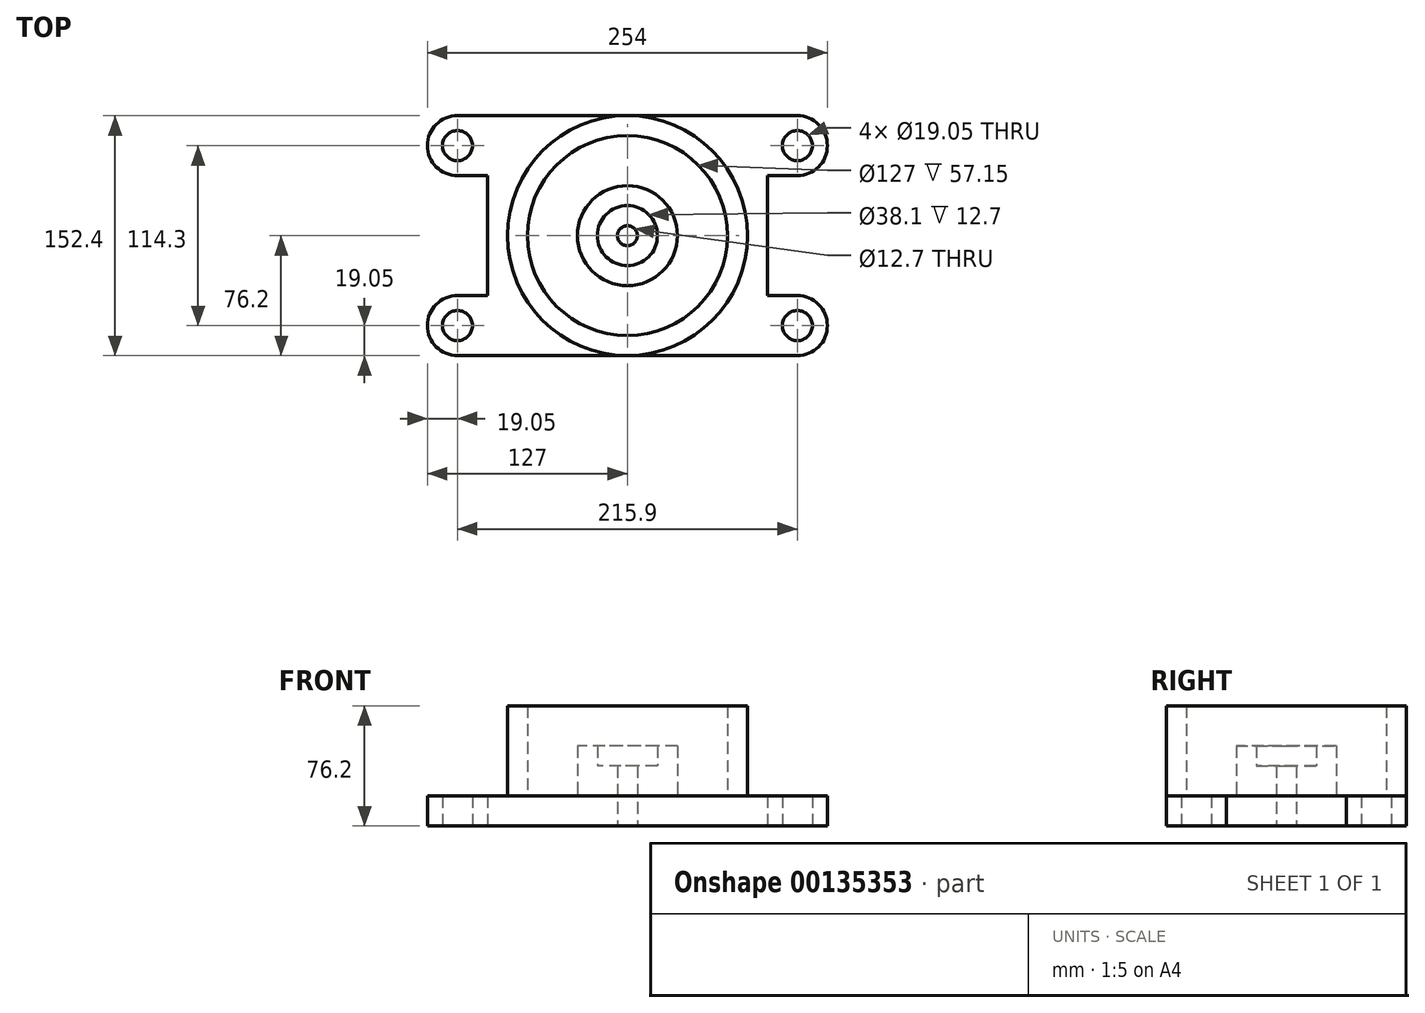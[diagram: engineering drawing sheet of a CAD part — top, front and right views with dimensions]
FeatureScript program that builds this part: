
annotation { "Feature Type Name" : "Feature", "Feature Type Description" : "" }
export const myFeature = defineFeature(function(context is Context, id is Id, definition is map)
    precondition{}
    {
        {
            var Q0;
            Q0=qCreatedBy(makeId("Top.planeOp"),FACE);
            var sketch = newSketch(context, id + "F0", { "sketchPlane" : qUnion([Q0])});
            skCircle(sketch, "E0", {"center": v(0, 0) * mm, "radius": 6.35 * mm});
            skCircle(sketch, "E1", {"center": v(0, 0) * mm, "radius": 19.05 * mm});
            skCircle(sketch, "E2", {"center": v(0, 0) * mm, "radius": 31.75 * mm});
            skCircle(sketch, "E3", {"center": v(0, 0) * mm, "radius": 63.5 * mm});
            skCircle(sketch, "E4", {"center": v(0, 0) * mm, "radius": 76.2 * mm});
            skLineSegment(sketch, "E5", {"start": v(0, -76.2) * mm, "end": v(-107.95, -76.2) * mm});
            skLineSegment(sketch, "E6", {"start": v(0, 76.2) * mm, "end": v(-107.95, 76.2) * mm});
            skLineSegment(sketch, "E7", {"start": v(0, 76.2) * mm, "end": v(107.95, 76.2) * mm});
            skLineSegment(sketch, "E8", {"start": v(0, -76.2) * mm, "end": v(107.95, -76.2) * mm});
            skArc(sketch, "E9", {"start": v(-107.95, 76.2) * mm, "mid": v(-127, 57.15) * mm, "end": v(-107.95, 38.1) * mm});
            skArc(sketch, "E10", {"start": v(-107.95, -38.1) * mm, "mid": v(-127, -57.15) * mm, "end": v(-107.95, -76.2) * mm});
            skArc(sketch, "E11", {"start": v(107.95, 38.1) * mm, "mid": v(127, 57.15) * mm, "end": v(107.95, 76.2) * mm});
            skArc(sketch, "E12", {"start": v(107.95, -76.2) * mm, "mid": v(127, -57.15) * mm, "end": v(107.95, -38.1) * mm});
            skLineSegment(sketch, "E13", {"start": v(-107.95, 38.1) * mm, "end": v(-88.9, 38.1) * mm});
            skLineSegment(sketch, "E14", {"start": v(-107.95, -38.1) * mm, "end": v(-88.9, -38.1) * mm});
            skLineSegment(sketch, "E15", {"start": v(-88.9, -38.1) * mm, "end": v(-88.9, 38.1) * mm});
            skLineSegment(sketch, "E16", {"start": v(107.95, 38.1) * mm, "end": v(88.9, 38.1) * mm});
            skLineSegment(sketch, "E17", {"start": v(107.95, -38.1) * mm, "end": v(88.9, -38.1) * mm});
            skLineSegment(sketch, "E18", {"start": v(88.9, 38.1) * mm, "end": v(88.9, -38.1) * mm});
            skCircle(sketch, "E19", {"center": v(-107.95, 57.15) * mm, "radius": 9.53 * mm});
            skCircle(sketch, "E20", {"center": v(-107.95, -57.15) * mm, "radius": 9.53 * mm});
            skCircle(sketch, "E21", {"center": v(107.95, -57.15) * mm, "radius": 9.53 * mm});
            skCircle(sketch, "E22", {"center": v(107.95, 57.15) * mm, "radius": 9.53 * mm});
            skSolve(sketch);
        }
        {
            var Q0;
            {var subQ1=sQuery(id+"F0.wireOp",EDGE,"E5");Q0=makeQuery(id+"F0.imprint","IMPRINT",FACE,{"disambiguationData":[TD([[makeQuery(id+"F0.imprint","IMPRINT",EDGE,{"derivedFrom":subQ1}),-1.0]])]});}
            var Q1;
            {var subQ2=sQuery(id+"F0.wireOp",EDGE,"E7");Q1=makeQuery(id+"F0.imprint","IMPRINT",FACE,{"disambiguationData":[TD([[makeQuery(id+"F0.imprint","IMPRINT",EDGE,{"derivedFrom":subQ2}),-1.0]])]});}
            extrude(context, id + "F1", {"entities" : qUnion([Q0, Q1]), "depth" : 19.05 * mm});
        }
        {
            var Q0;
            Q0=makeQuery(id+"F0.imprint","IMPRINT",FACE,{"disambiguationData":[TD([[makeQuery(id+"F0.imprint","IMPRINT",EDGE,{"derivedFrom":sQuery(id+"F0.wireOp",EDGE,"E3")}),-1.0]])]});
            extrude(context, id + "F2", {"entities" : qUnion([Q0]), "operationType" : NewBodyOperationType.ADD, "depth" : 76.2 * mm});
        }
        {
            var Q0;
            Q0=makeQuery(id+"F0.imprint","IMPRINT",FACE,{"disambiguationData":[TD([[makeQuery(id+"F0.imprint","IMPRINT",EDGE,{"derivedFrom":sQuery(id+"F0.wireOp",EDGE,"E2")}),-1.0]])]});
            extrude(context, id + "F3", {"entities" : qUnion([Q0]), "operationType" : NewBodyOperationType.ADD, "depth" : 19.05 * mm});
        }
        {
            var Q0;
            Q0=makeQuery(id+"F0.imprint","IMPRINT",FACE,{"disambiguationData":[TD([[makeQuery(id+"F0.imprint","IMPRINT",EDGE,{"derivedFrom":sQuery(id+"F0.wireOp",EDGE,"E1")}),-1.0]])]});
            extrude(context, id + "F4", {"entities" : qUnion([Q0]), "operationType" : NewBodyOperationType.ADD, "depth" : 50.8 * mm});
        }
        {
            var Q0;
            Q0=makeQuery(id+"F0.imprint","IMPRINT",FACE,{"disambiguationData":[TD([[makeQuery(id+"F0.imprint","IMPRINT",EDGE,{"derivedFrom":sQuery(id+"F0.wireOp",EDGE,"E0")}),-1.0]])]});
            extrude(context, id + "F5", {"entities" : qUnion([Q0]), "operationType" : NewBodyOperationType.ADD, "depth" : 38.1 * mm});
        }
    });
